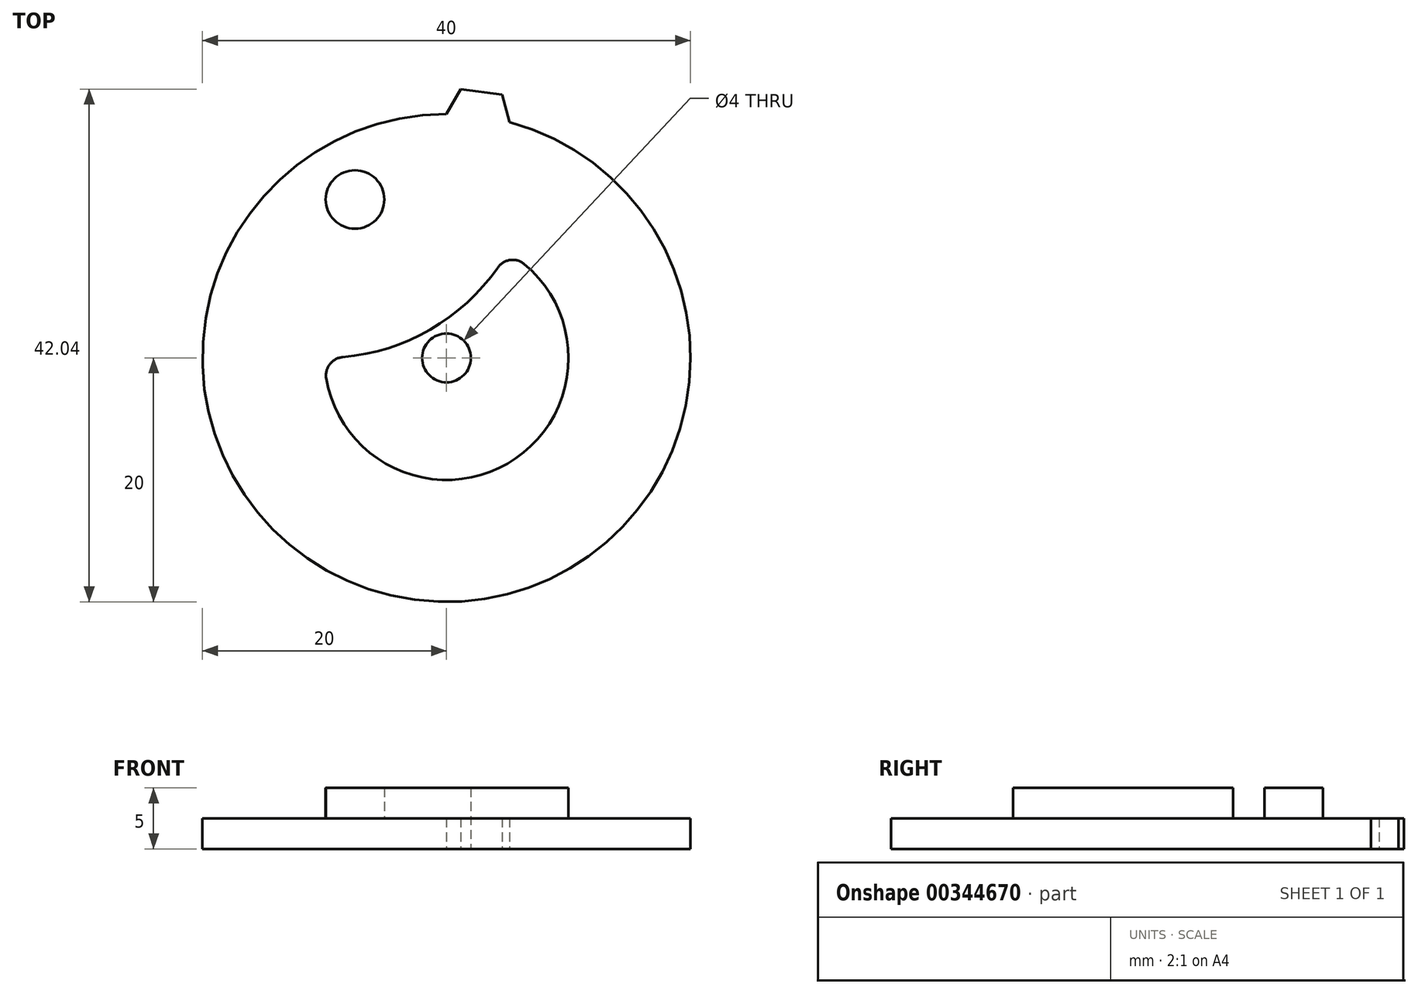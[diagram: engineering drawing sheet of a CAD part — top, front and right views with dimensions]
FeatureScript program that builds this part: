
annotation { "Feature Type Name" : "Feature", "Feature Type Description" : "" }
export const myFeature = defineFeature(function(context is Context, id is Id, definition is map)
    precondition{}
    {
        {
            var Q0;
            Q0=qCreatedBy(makeId("Top.planeOp"),FACE);
            var sketch = newSketch(context, id + "F0", { "sketchPlane" : qUnion([Q0])});
            skLineSegment(sketch, "E0", {"start": v(0, 0) * mm, "end": v(22.5, 13) * mm, "construction": true});
            skLineSegment(sketch, "E1", {"start": v(22.5, 13) * mm, "end": v(30, 0) * mm});
            skLineSegment(sketch, "E2", {"start": v(30, 0) * mm, "end": v(0, 0) * mm, "construction": true});
            skCircle(sketch, "E3", {"center": v(0, 0) * mm, "radius": 25.98 * mm, "construction": true});
            skLineSegment(sketch, "E4", {"start": v(30, 0) * mm, "end": v(20, 17.32) * mm, "construction": true});
            skLineSegment(sketch, "E5", {"start": v(20, 17.32) * mm, "end": v(20, 0) * mm, "construction": true});
            skCircle(sketch, "E6", {"center": v(30, 0) * mm, "radius": 10 * mm, "construction": true});
            skCircle(sketch, "E7", {"center": v(22.5, 13) * mm, "radius": 2.4 * mm});
            skArc(sketch, "E8", {"start": v(20, 0) * mm, "mid": v(28.66, 2.32) * mm, "end": v(35, 8.66) * mm});
            skArc(sketch, "E9", {"start": v(20, 0) * mm, "mid": v(35, -8.66) * mm, "end": v(35, 8.66) * mm});
            skCircle(sketch, "E10", {"center": v(30, 0) * mm, "radius": 20 * mm});
            skCircle(sketch, "E11", {"center": v(30, 0) * mm, "radius": 2 * mm});
            skSolve(sketch);
        }
        {
            var Q0;
            Q0=qCreatedBy(makeId("Top.planeOp"),FACE);
            var sketch = newSketch(context, id + "F1", { "sketchPlane" : qUnion([Q0])});
            skLineSegment(sketch, "E12", {"start": v(0, 0) * mm, "end": v(30, 0) * mm});
            skCircle(sketch, "E13", {"center": v(30, 0) * mm, "radius": 20 * mm, "construction": true});
            skLineSegment(sketch, "E14", {"start": v(30, 0) * mm, "end": v(30, 20) * mm, "construction": true});
            skLineSegment(sketch, "E15", {"start": v(30, 0) * mm, "end": v(35.18, 19.32) * mm, "construction": true});
            skLineSegment(sketch, "E16", {"start": v(30, 20) * mm, "end": v(31.17, 22.04) * mm});
            skLineSegment(sketch, "E17", {"start": v(34.57, 21.59) * mm, "end": v(35.18, 19.32) * mm});
            skLineSegment(sketch, "E18", {"start": v(30, 0) * mm, "end": v(32.87, 21.81) * mm, "construction": true});
            skLineSegment(sketch, "E19", {"start": v(31.17, 22.04) * mm, "end": v(32.87, 21.81) * mm});
            skLineSegment(sketch, "E20", {"start": v(34.57, 21.59) * mm, "end": v(32.87, 21.81) * mm});
            skArc(sketch, "E21", {"start": v(30, 20) * mm, "mid": v(32.61, 19.83) * mm, "end": v(35.18, 19.32) * mm});
            skLineSegment(sketch, "E22.1.0", {"start": v(24.82, 19.32) * mm, "end": v(25.43, 21.59) * mm});
            skLineSegment(sketch, "E22.1.1", {"start": v(25.43, 21.59) * mm, "end": v(27.13, 21.81) * mm});
            skLineSegment(sketch, "E22.1.2", {"start": v(28.83, 22.04) * mm, "end": v(27.13, 21.81) * mm});
            skLineSegment(sketch, "E22.1.3", {"start": v(28.83, 22.04) * mm, "end": v(30, 20) * mm});
            skLineSegment(sketch, "E22.2.0", {"start": v(20, 17.32) * mm, "end": v(20, 19.67) * mm});
            skLineSegment(sketch, "E22.2.1", {"start": v(20, 19.67) * mm, "end": v(21.58, 20.33) * mm});
            skLineSegment(sketch, "E22.2.2", {"start": v(23.16, 20.98) * mm, "end": v(21.58, 20.33) * mm});
            skLineSegment(sketch, "E22.2.3", {"start": v(23.16, 20.98) * mm, "end": v(24.82, 19.32) * mm});
            skLineSegment(sketch, "E22.3.0", {"start": v(15.86, 14.14) * mm, "end": v(15.25, 16.41) * mm});
            skLineSegment(sketch, "E22.3.1", {"start": v(15.25, 16.41) * mm, "end": v(16.6, 17.45) * mm});
            skLineSegment(sketch, "E22.3.2", {"start": v(17.96, 18.5) * mm, "end": v(16.6, 17.45) * mm});
            skLineSegment(sketch, "E22.3.3", {"start": v(17.96, 18.5) * mm, "end": v(20, 17.32) * mm});
            skLineSegment(sketch, "E22.4.0", {"start": v(12.68, 10) * mm, "end": v(11.5, 12.04) * mm});
            skLineSegment(sketch, "E22.4.1", {"start": v(11.5, 12.04) * mm, "end": v(12.55, 13.4) * mm});
            skLineSegment(sketch, "E22.4.2", {"start": v(13.59, 14.75) * mm, "end": v(12.55, 13.4) * mm});
            skLineSegment(sketch, "E22.4.3", {"start": v(13.59, 14.75) * mm, "end": v(15.86, 14.14) * mm});
            skLineSegment(sketch, "E22.5.0", {"start": v(10.68, 5.18) * mm, "end": v(9.02, 6.84) * mm});
            skLineSegment(sketch, "E22.5.1", {"start": v(9.02, 6.84) * mm, "end": v(9.67, 8.42) * mm});
            skLineSegment(sketch, "E22.5.2", {"start": v(10.33, 10) * mm, "end": v(9.67, 8.42) * mm});
            skLineSegment(sketch, "E22.5.3", {"start": v(10.33, 10) * mm, "end": v(12.68, 10) * mm});
            skLineSegment(sketch, "E22.6.0", {"start": v(10, 0) * mm, "end": v(7.96, 1.17) * mm});
            skLineSegment(sketch, "E22.6.1", {"start": v(7.96, 1.17) * mm, "end": v(8.19, 2.87) * mm});
            skLineSegment(sketch, "E22.6.2", {"start": v(8.41, 4.57) * mm, "end": v(8.19, 2.87) * mm});
            skLineSegment(sketch, "E22.6.3", {"start": v(8.41, 4.57) * mm, "end": v(10.68, 5.18) * mm});
            skLineSegment(sketch, "E22.7.0", {"start": v(10.68, -5.18) * mm, "end": v(8.41, -4.57) * mm});
            skLineSegment(sketch, "E22.7.1", {"start": v(8.41, -4.57) * mm, "end": v(8.19, -2.87) * mm});
            skLineSegment(sketch, "E22.7.2", {"start": v(7.96, -1.17) * mm, "end": v(8.19, -2.87) * mm});
            skLineSegment(sketch, "E22.7.3", {"start": v(7.96, -1.17) * mm, "end": v(10, 0) * mm});
            skLineSegment(sketch, "E22.8.0", {"start": v(12.68, -10) * mm, "end": v(10.33, -10) * mm});
            skLineSegment(sketch, "E22.8.1", {"start": v(10.33, -10) * mm, "end": v(9.67, -8.42) * mm});
            skLineSegment(sketch, "E22.8.2", {"start": v(9.02, -6.84) * mm, "end": v(9.67, -8.42) * mm});
            skLineSegment(sketch, "E22.8.3", {"start": v(9.02, -6.84) * mm, "end": v(10.68, -5.18) * mm});
            skLineSegment(sketch, "E22.9.0", {"start": v(15.86, -14.14) * mm, "end": v(13.59, -14.75) * mm});
            skLineSegment(sketch, "E22.9.1", {"start": v(13.59, -14.75) * mm, "end": v(12.55, -13.4) * mm});
            skLineSegment(sketch, "E22.9.2", {"start": v(11.5, -12.04) * mm, "end": v(12.55, -13.4) * mm});
            skLineSegment(sketch, "E22.9.3", {"start": v(11.5, -12.04) * mm, "end": v(12.68, -10) * mm});
            skLineSegment(sketch, "E22.10.0", {"start": v(20, -17.32) * mm, "end": v(17.96, -18.5) * mm});
            skLineSegment(sketch, "E22.10.1", {"start": v(17.96, -18.5) * mm, "end": v(16.6, -17.45) * mm});
            skLineSegment(sketch, "E22.10.2", {"start": v(15.25, -16.41) * mm, "end": v(16.6, -17.45) * mm});
            skLineSegment(sketch, "E22.10.3", {"start": v(15.25, -16.41) * mm, "end": v(15.86, -14.14) * mm});
            skLineSegment(sketch, "E22.11.0", {"start": v(24.82, -19.32) * mm, "end": v(23.16, -20.98) * mm});
            skLineSegment(sketch, "E22.11.1", {"start": v(23.16, -20.98) * mm, "end": v(21.58, -20.33) * mm});
            skLineSegment(sketch, "E22.11.2", {"start": v(20, -19.67) * mm, "end": v(21.58, -20.33) * mm});
            skLineSegment(sketch, "E22.11.3", {"start": v(20, -19.67) * mm, "end": v(20, -17.32) * mm});
            skLineSegment(sketch, "E22.12.0", {"start": v(30, -20) * mm, "end": v(28.83, -22.04) * mm});
            skLineSegment(sketch, "E22.12.1", {"start": v(28.83, -22.04) * mm, "end": v(27.13, -21.81) * mm});
            skLineSegment(sketch, "E22.12.2", {"start": v(25.43, -21.59) * mm, "end": v(27.13, -21.81) * mm});
            skLineSegment(sketch, "E22.12.3", {"start": v(25.43, -21.59) * mm, "end": v(24.82, -19.32) * mm});
            skLineSegment(sketch, "E22.13.0", {"start": v(35.18, -19.32) * mm, "end": v(34.57, -21.59) * mm});
            skLineSegment(sketch, "E22.13.1", {"start": v(34.57, -21.59) * mm, "end": v(32.87, -21.81) * mm});
            skLineSegment(sketch, "E22.13.2", {"start": v(31.17, -22.04) * mm, "end": v(32.87, -21.81) * mm});
            skLineSegment(sketch, "E22.13.3", {"start": v(31.17, -22.04) * mm, "end": v(30, -20) * mm});
            skLineSegment(sketch, "E22.14.0", {"start": v(40, -17.32) * mm, "end": v(40, -19.67) * mm});
            skLineSegment(sketch, "E22.14.1", {"start": v(40, -19.67) * mm, "end": v(38.42, -20.33) * mm});
            skLineSegment(sketch, "E22.14.2", {"start": v(36.84, -20.98) * mm, "end": v(38.42, -20.33) * mm});
            skLineSegment(sketch, "E22.14.3", {"start": v(36.84, -20.98) * mm, "end": v(35.18, -19.32) * mm});
            skLineSegment(sketch, "E22.15.0", {"start": v(44.14, -14.14) * mm, "end": v(44.75, -16.41) * mm});
            skLineSegment(sketch, "E22.15.1", {"start": v(44.75, -16.41) * mm, "end": v(43.4, -17.45) * mm});
            skLineSegment(sketch, "E22.15.2", {"start": v(42.04, -18.5) * mm, "end": v(43.4, -17.45) * mm});
            skLineSegment(sketch, "E22.15.3", {"start": v(42.04, -18.5) * mm, "end": v(40, -17.32) * mm});
            skLineSegment(sketch, "E22.16.0", {"start": v(47.32, -10) * mm, "end": v(48.5, -12.04) * mm});
            skLineSegment(sketch, "E22.16.1", {"start": v(48.5, -12.04) * mm, "end": v(47.45, -13.4) * mm});
            skLineSegment(sketch, "E22.16.2", {"start": v(46.41, -14.75) * mm, "end": v(47.45, -13.4) * mm});
            skLineSegment(sketch, "E22.16.3", {"start": v(46.41, -14.75) * mm, "end": v(44.14, -14.14) * mm});
            skLineSegment(sketch, "E22.17.0", {"start": v(49.32, -5.18) * mm, "end": v(50.98, -6.84) * mm});
            skLineSegment(sketch, "E22.17.1", {"start": v(50.98, -6.84) * mm, "end": v(50.33, -8.42) * mm});
            skLineSegment(sketch, "E22.17.2", {"start": v(49.67, -10) * mm, "end": v(50.33, -8.42) * mm});
            skLineSegment(sketch, "E22.17.3", {"start": v(49.67, -10) * mm, "end": v(47.32, -10) * mm});
            skLineSegment(sketch, "E22.18.0", {"start": v(50, 0) * mm, "end": v(52.04, -1.17) * mm});
            skLineSegment(sketch, "E22.18.1", {"start": v(52.04, -1.17) * mm, "end": v(51.81, -2.87) * mm});
            skLineSegment(sketch, "E22.18.2", {"start": v(51.59, -4.57) * mm, "end": v(51.81, -2.87) * mm});
            skLineSegment(sketch, "E22.18.3", {"start": v(51.59, -4.57) * mm, "end": v(49.32, -5.18) * mm});
            skLineSegment(sketch, "E22.19.0", {"start": v(49.32, 5.18) * mm, "end": v(51.59, 4.57) * mm});
            skLineSegment(sketch, "E22.19.1", {"start": v(51.59, 4.57) * mm, "end": v(51.81, 2.87) * mm});
            skLineSegment(sketch, "E22.19.2", {"start": v(52.04, 1.17) * mm, "end": v(51.81, 2.87) * mm});
            skLineSegment(sketch, "E22.19.3", {"start": v(52.04, 1.17) * mm, "end": v(50, 0) * mm});
            skLineSegment(sketch, "E22.20.0", {"start": v(47.32, 10) * mm, "end": v(49.67, 10) * mm});
            skLineSegment(sketch, "E22.20.1", {"start": v(49.67, 10) * mm, "end": v(50.33, 8.42) * mm});
            skLineSegment(sketch, "E22.20.2", {"start": v(50.98, 6.84) * mm, "end": v(50.33, 8.42) * mm});
            skLineSegment(sketch, "E22.20.3", {"start": v(50.98, 6.84) * mm, "end": v(49.32, 5.18) * mm});
            skLineSegment(sketch, "E22.21.0", {"start": v(44.14, 14.14) * mm, "end": v(46.41, 14.75) * mm});
            skLineSegment(sketch, "E22.21.1", {"start": v(46.41, 14.75) * mm, "end": v(47.45, 13.4) * mm});
            skLineSegment(sketch, "E22.21.2", {"start": v(48.5, 12.04) * mm, "end": v(47.45, 13.4) * mm});
            skLineSegment(sketch, "E22.21.3", {"start": v(48.5, 12.04) * mm, "end": v(47.32, 10) * mm});
            skLineSegment(sketch, "E22.22.0", {"start": v(40, 17.32) * mm, "end": v(42.04, 18.5) * mm});
            skLineSegment(sketch, "E22.22.1", {"start": v(42.04, 18.5) * mm, "end": v(43.4, 17.45) * mm});
            skLineSegment(sketch, "E22.22.2", {"start": v(44.75, 16.41) * mm, "end": v(43.4, 17.45) * mm});
            skLineSegment(sketch, "E22.22.3", {"start": v(44.75, 16.41) * mm, "end": v(44.14, 14.14) * mm});
            skLineSegment(sketch, "E22.23.0", {"start": v(35.18, 19.32) * mm, "end": v(36.84, 20.98) * mm});
            skLineSegment(sketch, "E22.23.1", {"start": v(36.84, 20.98) * mm, "end": v(38.42, 20.33) * mm});
            skLineSegment(sketch, "E22.23.2", {"start": v(40, 19.67) * mm, "end": v(38.42, 20.33) * mm});
            skLineSegment(sketch, "E22.23.3", {"start": v(40, 19.67) * mm, "end": v(40, 17.32) * mm});
            skCircle(sketch, "E23", {"center": v(30, 0) * mm, "radius": 2 * mm});
            skSolve(sketch);
        }
        {
            var Q0;
            Q0=makeQuery(id+"F0.imprint","IMPRINT",FACE,{"disambiguationData":[TD([[makeQuery(id+"F0.imprint","IMPRINT",EDGE,{"derivedFrom":sQuery(id+"F0.wireOp",EDGE,"E7")}),-1.0]])]});
            extrude(context, id + "F2", {"entities" : qUnion([Q0]), "depth" : 2.5 * mm});
        }
        {
            var Q0;
            Q0=makeQuery(id+"F0.imprint","IMPRINT",FACE,{"disambiguationData":[TD([[makeQuery(id+"F0.imprint","IMPRINT",EDGE,{"derivedFrom":sQuery(id+"F0.wireOp",EDGE,"E7")}),1.0]])]});
            var Q1;
            {var subQ0=sQuery(id+"F0.wireOp",EDGE,"E9");Q1=makeQuery(id+"F0.imprint","IMPRINT",FACE,{"disambiguationData":[TD([[makeQuery(id+"F0.imprint","IMPRINT",EDGE,{"derivedFrom":subQ0}),1.0]])]});}
            extrude(context, id + "F3", {"entities" : qUnion([Q0, Q1]), "operationType" : NewBodyOperationType.ADD, "depth" : 5 * mm});
        }
        {
            var Q0;
            Q0=makeQuery(id+"F1.imprint","IMPRINT",FACE,{"disambiguationData":[TD([[makeQuery(id+"F1.imprint","IMPRINT",EDGE,{"derivedFrom":sQuery(id+"F1.wireOp",EDGE,"E16")}),-1.0]])]});
            var Q1;
            Q1=makeQuery(id+"F1.imprint","IMPRINT",FACE,{"disambiguationData":[TD([[makeQuery(id+"F1.imprint","IMPRINT",EDGE,{"derivedFrom":sQuery(id+"F1.wireOp",EDGE,"E21")}),-1.0]])]});
            extrude(context, id + "F4", {"entities" : qUnion([Q0, Q1]), "operationType" : NewBodyOperationType.ADD, "depth" : 2.5 * mm});
        }
        {
            var Q0;
            {var subQ0=sQuery(id+"F0.wireOp",EDGE,"E9");var subQ1=sQuery(id+"F0.wireOp",EDGE,"E8");Q0=makeQuery(id+"F3.opExtrude","SWEPT_EDGE",EDGE,{"disambiguationData":[OSD([subQ1,subQ0]),TDD([makeQuery(id+"F0.imprint","INTERSECT",VERTEX,{"disambiguationData":[OD(1.0)],"derivedFrom":[subQ1,subQ0]})])]});}
            var Q1;
            {var subQ0=sQuery(id+"F0.wireOp",EDGE,"E9");var subQ1=sQuery(id+"F0.wireOp",EDGE,"E8");Q1=makeQuery(id+"F3.opExtrude","SWEPT_EDGE",EDGE,{"disambiguationData":[OSD([subQ1,subQ0]),TDD([makeQuery(id+"F0.imprint","INTERSECT",VERTEX,{"disambiguationData":[OD(0.0)],"derivedFrom":[subQ1,subQ0]})])]});}
            fillet(context, id + "F5", {"entities" : qUnion([Q0, Q1]), "radius" : 1.5 * mm, "tangentPropagation" : true, "allowEdgeOverflow" : false});
        }
    });
